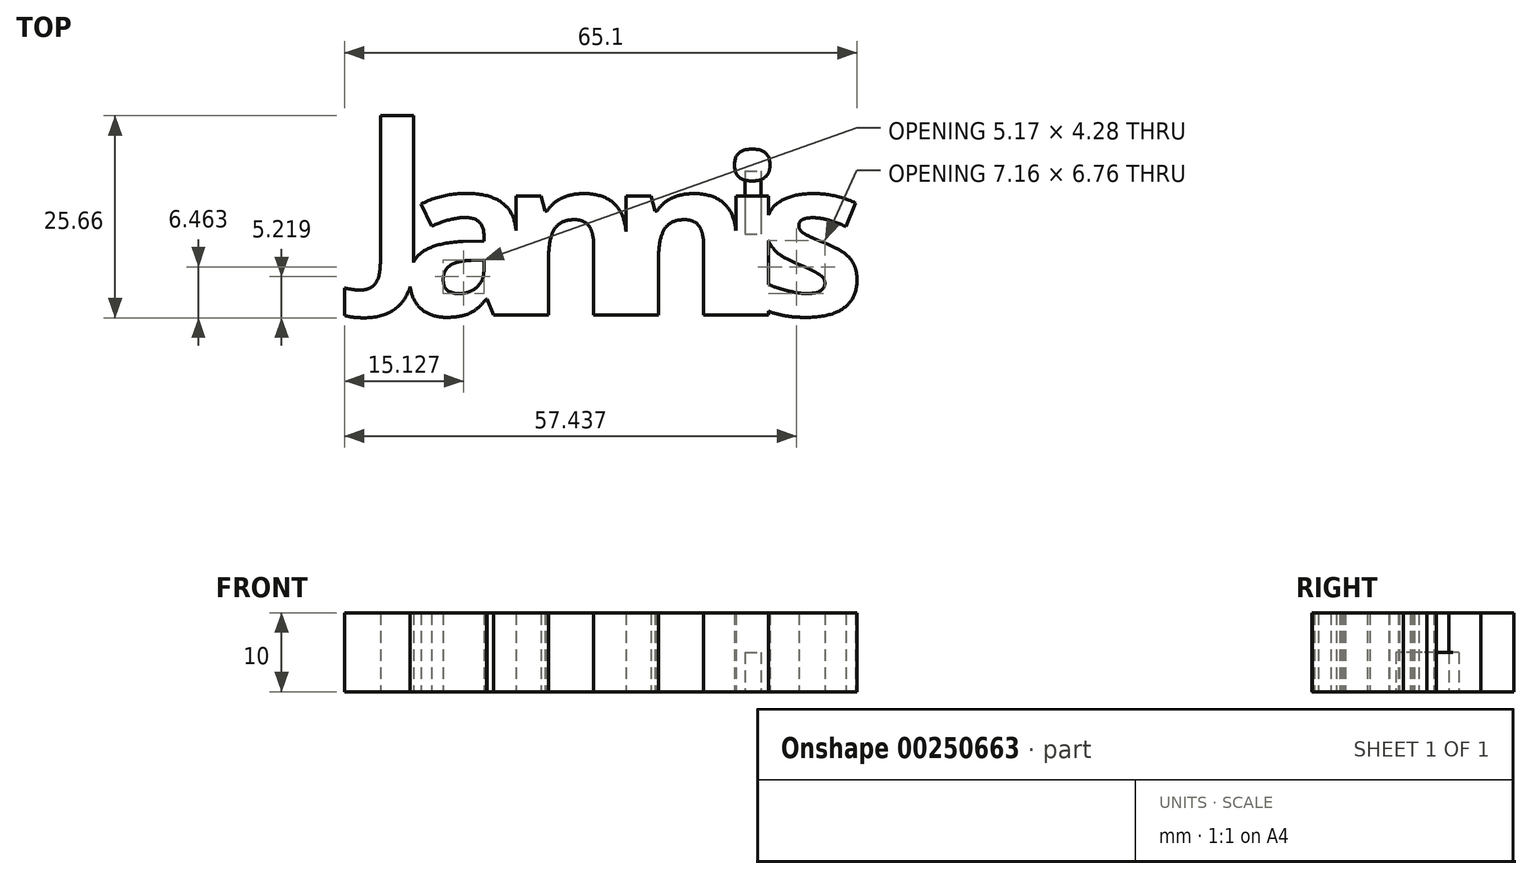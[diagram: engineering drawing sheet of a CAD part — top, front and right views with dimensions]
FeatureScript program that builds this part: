
annotation { "Feature Type Name" : "Feature", "Feature Type Description" : "" }
export const myFeature = defineFeature(function(context is Context, id is Id, definition is map)
    precondition{}
    {
        {
            var Q0;
            Q0=qCreatedBy(makeId("Top.planeOp"),FACE);
            var sketch = newSketch(context, id + "F0", { "sketchPlane" : qUnion([Q0])});
            skText(sketch, "E0", { "text": "J", "fontName": "OpenSans-Bold.ttf"});
            skText(sketch, "E1", { "text": "a", "fontName": "OpenSans-Bold.ttf"});
            skText(sketch, "E2", { "text": "n", "fontName": "OpenSans-Bold.ttf"});
            skText(sketch, "E3", { "text": "n", "fontName": "OpenSans-Bold.ttf"});
            skText(sketch, "E4", { "text": "i", "fontName": "OpenSans-Bold.ttf"});
            skText(sketch, "E5", { "text": "s", "fontName": "OpenSans-Bold.ttf"});
            const initialGuessF0  = {"E0": [-0.11764, 0.03076, 1, 0, 0.02], "E1": [-0.11257, 0.02526, 1, 0, 0.02], "E2": [-0.10008, 0.02526, 1, 0, 0.02], "E3": [-0.08611, 0.02526, 1, 0, 0.02], "E4": [-0.07215, 0.02526, 1, 0, 0.02], "E5": [-0.06735, 0.02526, 1, 0, 0.02]};
            skSetInitialGuess(sketch, initialGuessF0);
            skSolve(sketch);
        }
        {
            var Q0;
            Q0 = qSketchRegion(id + "F0", true);
            extrude(context, id + "F1", {"entities" : qUnion([Q0]), "depth" : 10 * mm});
        }
        {
            var Q0;
            Q0=qCreatedBy(makeId("Top.planeOp"),FACE);
            var sketch = newSketch(context, id + "F2", { "sketchPlane" : qUnion([Q0])});
            skLineSegment(sketch, "E6.bottom", {"start": v(-68.8, 43.57) * mm, "end": v(-66.8, 43.57) * mm});
            skLineSegment(sketch, "E6.top", {"start": v(-68.8, 35.57) * mm, "end": v(-66.8, 35.57) * mm});
            skLineSegment(sketch, "E6.left", {"start": v(-68.8, 43.57) * mm, "end": v(-68.8, 35.57) * mm});
            skLineSegment(sketch, "E6.right", {"start": v(-66.8, 43.57) * mm, "end": v(-66.8, 35.57) * mm});
            skSolve(sketch);
        }
        {
            var Q0;
            Q0 = qSketchRegion(id + "F2", true);
            extrude(context, id + "F3", {"entities" : qUnion([Q0]), "depth" : 5 * mm});
        }
    });
